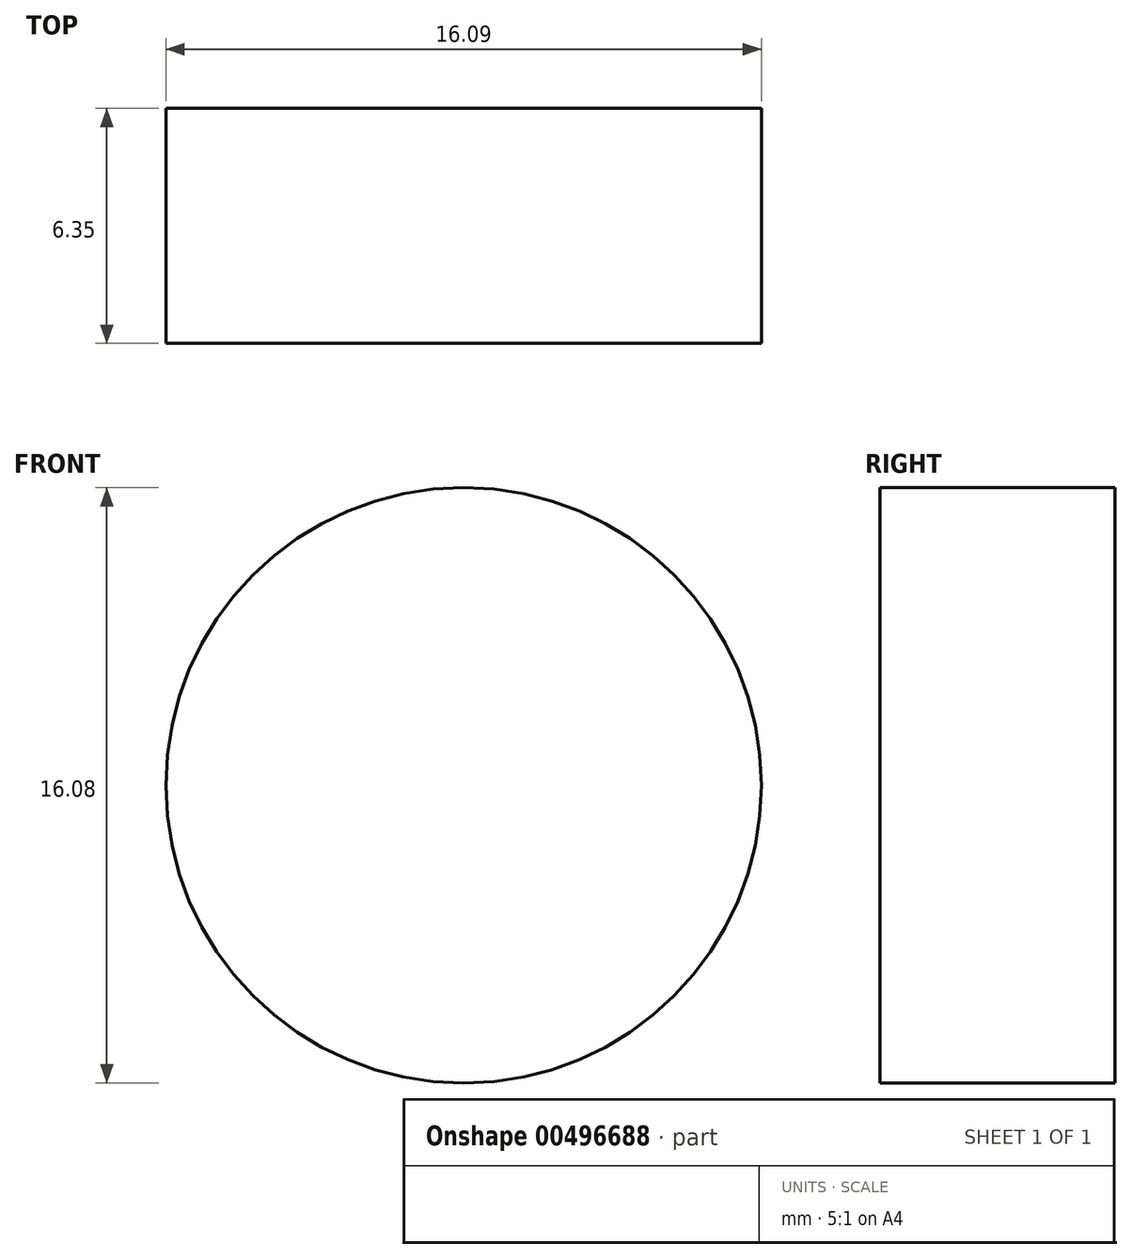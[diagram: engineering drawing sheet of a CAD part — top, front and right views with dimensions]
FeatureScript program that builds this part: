
annotation { "Feature Type Name" : "Feature", "Feature Type Description" : "" }
export const myFeature = defineFeature(function(context is Context, id is Id, definition is map)
    precondition{}
    {
        {
            var Q0;
            Q0=qCreatedBy(makeId("Front.planeOp"),FACE);
            var sketch = newSketch(context, id + "F0", { "sketchPlane" : qUnion([Q0])});
            skCircle(sketch, "E0", {"center": v(-48.79, 22.93) * mm, "radius": 8.04 * mm});
            skSolve(sketch);
        }
        {
            var Q0;
            Q0=makeQuery(id+"F0.imprint","IMPRINT",FACE,{"disambiguationData":[TD([[makeQuery(id+"F0.imprint","IMPRINT",EDGE,{"derivedFrom":sQuery(id+"F0.wireOp",EDGE,"E0")}),1.0]])]});
            extrude(context, id + "F1", {"entities" : qUnion([Q0]), "depth" : 6.35 * mm});
        }
    });
